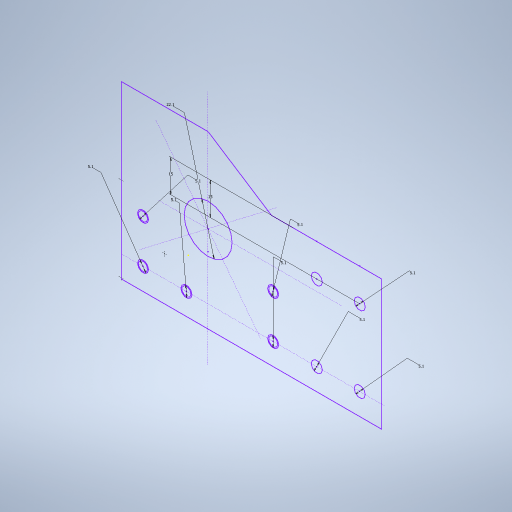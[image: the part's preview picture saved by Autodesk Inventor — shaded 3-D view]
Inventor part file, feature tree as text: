
AUTODESK INVENTOR PART (.ipt)
format: ipt  version: 2023.2 (Build 272271000, 271)  size: 258,560 bytes
history: native  units: mm
features: sketch x1
ambient origin geometry x8: Origin, YZ Plane, XZ Plane, XY Plane, X Axis, Y Axis, Z Axis, Center Point
feature tree (1):
  sketch  "Sketch1"  dims[d0=5.1mm d1=5.1mm d2=5.1mm d3=15.0mm d4=15.0mm d12=22.1mm d13=5.1mm d14=5.1mm d15=5.1mm d16=5.1mm d17=5.1mm]
